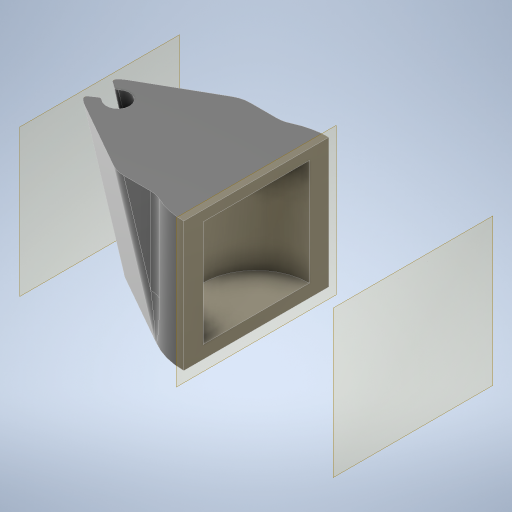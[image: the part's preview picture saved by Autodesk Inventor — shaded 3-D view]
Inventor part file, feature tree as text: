
AUTODESK INVENTOR PART (.ipt)
format: ipt  version: 2023 (Build 270158000, 158)  size: 427,520 bytes
history: native  units: in
note: dims shown in document units (in); Inventor stores cm internally (conversion verified against a paired STEP export)
features: sketch x6, extrude x5, plane x3, sweep x2, fillet x2, projected_geometry x1
ambient origin geometry x8: Origin, YZ Plane, XZ Plane, XY Plane, X Axis, Y Axis, Z Axis, Center Point
bodies: Body1 (feature_tree)
feature tree (19):
  sketch  "Sketch5"  dims[d48=0.56in d54=0.5in]
  sketch  "Sketch1"  dims[d21=0.2405in d22=0.2405in]
  sweep  "Sweep1"
  sweep  "Sweep2"
  extrude  "Extrusion4"  Depth=0.2405in
  extrude  "Extrusion5"  TaperAngle=0.0deg  [1 undecoded]
  fillet  "Fillet3"  [1 undecoded]
  fillet  "Fillet4"  Radius=0.5in
  extrude  "Extrusion6"  Depth=0.41in
  extrude  "Extrusion7"  Depth=0.01in
  plane  "Work Plane4"
  plane  "Work Plane6"
  extrude  "Extrusion8"  Depth=0.01in
  sketch  "Sketch7"  dims[d55=0.1202in d56=0.2405in]
  projected_geometry  "Projected Loop4"
  sketch  "Sketch8"  dims[d57=0.1202in d58=0.0in d59=0.0in d60=0.0in d61=0.0in d64=0.5in]
  sketch  "Sketch9"  dims[d65=0.0in d66=0.41in]
  sketch  "Sketch10"  dims[d67=0.45in d68=0.0in d69=0.01in d70=0.1in d71=0.04in d72=0.0in d73=0.04in d74=0.0in d75=1.0in d76=0.0in d15=0.0in d16=0.0in d17=0.0in d18=0.0in]
  plane  "Work Plane5"
note: 2 required parameter values undecoded (feature->parameter linkage not recoverable at this tier; creation-order binding heuristic only, values carry confidence <= 0.55)
